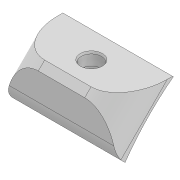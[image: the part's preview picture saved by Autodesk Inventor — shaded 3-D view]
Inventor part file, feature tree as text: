
AUTODESK INVENTOR PART (.ipt)
format: ipt  version: 2021 (Build 250183000, 183)  size: 248,320 bytes
history: native  units: mm
features: extrude x11, sketch x10, move_body x10, projected_geometry x6, direct_edit x5, delete_face x3, fillet x3, chamfer x3, plane x1
ambient origin geometry x8: Origin, YZ Plane, XZ Plane, XY Plane, X Axis, Y Axis, Z Axis, Center Point
bodies: Volumenkörper1 (feature_tree)
feature tree (52):
  extrude  "Extrusion1"  Depth=20.0mm TaperAngle=0.0deg
  extrude  "Extrusion2"  TaperAngle=0.0deg  [1 undecoded]
  plane  "Arbeitsebene1"
  extrude  "Extrusion3"  Depth=5.0mm TaperAngle=0.0deg
  extrude  "Extrusion4"  TaperAngle=0.0deg  [1 undecoded]
  extrude  "Extrusion6"  TaperAngle=0.0deg  [1 undecoded]
  extrude  "Extrusion7"  Depth=20.0mm TaperAngle=0.0deg
  direct_edit  "Direktbearbeitung1"
  direct_edit  "Direktbearbeitung2"
  direct_edit  "Direktbearbeitung3"
  sketch  "Skizze8"  dims[d23=0.0mm d24=0.0mm d25=20.0mm d26=0.0mm d27=0.0mm d28=1.5mm]
  extrude  "Extrusion8"  Depth=1.5mm TaperAngle=0.0deg
  extrude  "Extrusion9"  Depth=0.24265mm TaperAngle=0.0deg
  extrude  "Extrusion10"  Depth=15.6mm
  delete_face  "Fläche löschen1"
  direct_edit  "Direktbearbeitung4"
  extrude  "Extrusion11"  Depth=15.0mm TaperAngle=0.0deg
  extrude  "Extrusion12"  Depth=15.0mm TaperAngle=0.0deg
  delete_face  "Fläche löschen2"
  fillet  "Rundung2"  Radius=12.0mm
  chamfer  "Fase1"  Distance=6.0mm
  delete_face  "Fläche löschen3"
  chamfer  "Fase2"  [1 undecoded]
  chamfer  "Fase3"  [1 undecoded]
  fillet  "Rundung3"  [1 undecoded]
  direct_edit  "Direktbearbeitung5"
  fillet  "Rundung4"  Radius=20.0mm
  sketch  "Skizze1"  dims[d0=6.0mm d1=20.0mm d2=0.0mm]
  sketch  "Skizze2"  dims[d3=6.0mm d4=0.0mm d5=0.0mm]
  projected_geometry  "Projizierte Kontur1"
  sketch  "Skizze3"  dims[d6=-2.5mm d7=5.0mm d8=0.0mm]
  sketch  "Skizze4"  dims[d10=4.05mm d11=0.0mm d12=0.0mm]
  sketch  "Skizze6"  dims[d15=214.0mm d16=0.0mm d17=0.0mm]
  projected_geometry  "Projizierte Kontur3"
  sketch  "Skizze7"  dims[d18=5.0mm d19=0.0mm d20=0.0mm d21=0.0mm d22=20.0mm]
  projected_geometry  "Projizierte Kontur4"
  sketch  "Skizze9"  dims[d29=0.0mm d30=0.0mm d31=6.5mm d32=0.0mm d33=0.0mm d34=0.24265mm]
  projected_geometry  "Projizierte Kontur5"
  sketch  "Skizze10"  dims[d35=0.0mm d36=0.0mm d37=7.0mm d38=15.6mm]
  projected_geometry  "Projizierte Kontur6"
  projected_geometry  "Projizierte Kontur7"
  sketch  "Skizze11"  dims[d39=9.65mm d40=7.0mm d41=0.0mm d42=4.4mm d43=0.0mm d44=12.0mm d45=6.0mm d46=0.0mm d47=0.0mm d48=0.0mm d49=-0.5mm d50=0.0mm d51=0.0mm d52=-0.5mm d53=90.0deg d54=20.0mm d55=0.0mm d56=6.0mm d57=0.0mm d58=10.0mm d59=3.0mm d60=2.0mm d61=45.0deg d62=2.8mm d63=2.0mm d64=45.0deg d65=0.4mm d66=1.0mm d67=45.0deg d68=0.2mm d69=4.0mm d71=4.2mm d72=0.0mm d73=0.0mm d74=1.75mm d75=0.0mm d76=0.0mm d77=0.5mm d78=15.0mm]
  move_body  "Verschieben1"
  move_body  "Verschieben2"
  move_body  "Verschieben3"
  move_body  "Verschieben4"
  move_body  "Verschieben5"
  move_body  "Verschieben6"
  move_body  "Verschieben7"
  move_body  "Verschieben8"
  move_body  "Verschieben9"
  move_body  "Verschieben10"
note: 6 required parameter values undecoded (feature->parameter linkage not recoverable at this tier; creation-order binding heuristic only, values carry confidence <= 0.55)
